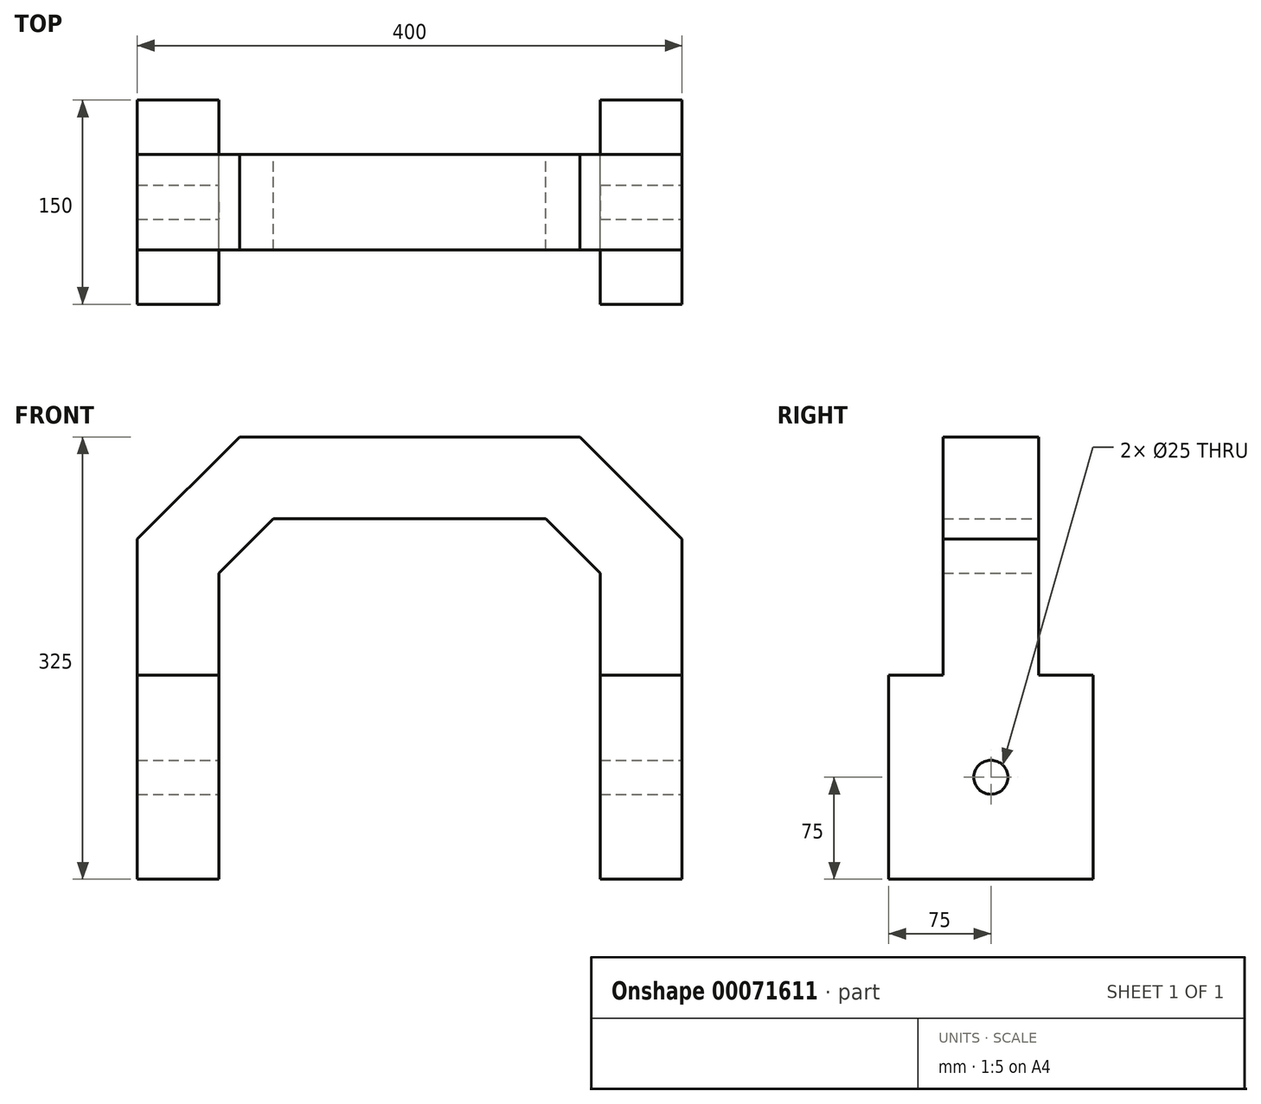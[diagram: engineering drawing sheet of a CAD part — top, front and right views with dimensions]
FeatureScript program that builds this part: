
annotation { "Feature Type Name" : "Feature", "Feature Type Description" : "" }
export const myFeature = defineFeature(function(context is Context, id is Id, definition is map)
    precondition{}
    {
        {
            var Q0;
            Q0=qCreatedBy(makeId("Front.planeOp"),FACE);
            var sketch = newSketch(context, id + "F0", { "sketchPlane" : qUnion([Q0])});
            skLineSegment(sketch, "E0", {"start": v(-140, 0) * mm, "end": v(-140, 150) * mm});
            skLineSegment(sketch, "E1", {"start": v(-140, 150) * mm, "end": v(-100, 190) * mm});
            skLineSegment(sketch, "E2", {"start": v(-100, 190) * mm, "end": v(100, 190) * mm});
            skLineSegment(sketch, "E3", {"start": v(100, 190) * mm, "end": v(140, 150) * mm});
            skLineSegment(sketch, "E4", {"start": v(140, 150) * mm, "end": v(140, 0) * mm});
            skLineSegment(sketch, "E5", {"start": v(140, 0) * mm, "end": v(200, 0) * mm});
            skLineSegment(sketch, "E6", {"start": v(200, 0) * mm, "end": v(200, 174.85) * mm});
            skLineSegment(sketch, "E7", {"start": v(200, 250) * mm, "end": v(124.85, 250) * mm, "construction": true});
            skLineSegment(sketch, "E8", {"start": v(-200, 0) * mm, "end": v(-140, 0) * mm});
            skLineSegment(sketch, "E9", {"start": v(-140, 0) * mm, "end": v(140, 0) * mm, "construction": true});
            skLineSegment(sketch, "E10", {"start": v(0, 0) * mm, "end": v(0, 190) * mm, "construction": true});
            skLineSegment(sketch, "E11", {"start": v(-140, 150) * mm, "end": v(140, 150) * mm, "construction": true});
            skLineSegment(sketch, "E12", {"start": v(-124.85, 250) * mm, "end": v(-200, 250) * mm, "construction": true});
            skLineSegment(sketch, "E13", {"start": v(-200, 174.85) * mm, "end": v(-200, 0) * mm});
            skLineSegment(sketch, "E14", {"start": v(124.85, 250) * mm, "end": v(-124.85, 250) * mm});
            skLineSegment(sketch, "E15", {"start": v(200, 174.85) * mm, "end": v(200, 250) * mm, "construction": true});
            skLineSegment(sketch, "E16", {"start": v(124.85, 250) * mm, "end": v(200, 174.85) * mm});
            skLineSegment(sketch, "E17", {"start": v(-200, 174.85) * mm, "end": v(-124.85, 250) * mm});
            skLineSegment(sketch, "E18", {"start": v(-200, 174.85) * mm, "end": v(-200, 250) * mm, "construction": true});
            skLineSegment(sketch, "E19", {"start": v(0, 190) * mm, "end": v(0, 250) * mm, "construction": true});
            skLineSegment(sketch, "E20", {"start": v(-100, 190) * mm, "end": v(-142.43, 232.43) * mm, "construction": true});
            skSolve(sketch);
        }
        {
            var Q0;
            Q0 = qSketchRegion(id + "F0", true);
            extrude(context, id + "F1", {"entities" : qUnion([Q0]), "depth" : 70 * mm});
        }
        {
            var Q0;
            Q0=makeQuery(id+"F1.opExtrude","SWEPT_FACE",FACE,{"disambiguationData":[OSD([sQuery(id+"F0.wireOp",EDGE,"E6")])]});
            var sketch = newSketch(context, id + "F2", { "sketchPlane" : qUnion([Q0])});
            skLineSegment(sketch, "E21.rect.bottom", {"start": v(40, -75) * mm, "end": v(-110, -75) * mm});
            skLineSegment(sketch, "E21.rect.top", {"start": v(40, 75) * mm, "end": v(-110, 75) * mm});
            skLineSegment(sketch, "E21.rect.left", {"start": v(40, -75) * mm, "end": v(40, 75) * mm});
            skLineSegment(sketch, "E21.rect.right", {"start": v(-110, -75) * mm, "end": v(-110, 75) * mm});
            skPoint(sketch, "E21.rect.middle", {"position": v(-35, 0) * mm});
            skSolve(sketch);
        }
        {
            var Q0;
            Q0 = qSketchRegion(id + "F2", true);
            var Q1;
            Q1=makeQuery(id+"F1.opExtrude","SWEPT_FACE",FACE,{"disambiguationData":[OSD([sQuery(id+"F0.wireOp",EDGE,"E4")])]});
            extrude(context, id + "F3", {"entities" : qUnion([Q0]), "operationType" : NewBodyOperationType.ADD, "endBound" : BoundingType.UP_TO_SURFACE, "oppositeDirection" : true, "endBoundEntityFace" : qUnion([Q1]), "depth" : 60 * mm});
        }
        {
            var Q0;
            Q0=makeQuery(id+"F1.opExtrude","SWEPT_FACE",FACE,{"disambiguationData":[OSD([sQuery(id+"F0.wireOp",EDGE,"E13")])]});
            var sketch = newSketch(context, id + "F4", { "sketchPlane" : qUnion([Q0])});
            skLineSegment(sketch, "E22.bottom", {"start": v(-40, 75) * mm, "end": v(110, 75) * mm});
            skLineSegment(sketch, "E22.top", {"start": v(-40, -75) * mm, "end": v(110, -75) * mm});
            skLineSegment(sketch, "E22.left", {"start": v(-40, 75) * mm, "end": v(-40, -75) * mm});
            skLineSegment(sketch, "E22.right", {"start": v(110, 75) * mm, "end": v(110, -75) * mm});
            skSolve(sketch);
        }
        {
            var Q0;
            Q0 = qSketchRegion(id + "F4", true);
            var Q1;
            Q1=makeQuery(id+"F1.opExtrude","SWEPT_FACE",FACE,{"disambiguationData":[OSD([sQuery(id+"F0.wireOp",EDGE,"E0")])]});
            extrude(context, id + "F5", {"entities" : qUnion([Q0]), "operationType" : NewBodyOperationType.ADD, "endBound" : BoundingType.UP_TO_SURFACE, "oppositeDirection" : true, "endBoundEntityFace" : qUnion([Q1]), "depth" : 25 * mm});
        }
        {
            var Q0;
            Q0=makeQuery(id+"F3.boolean.opBoolean","MERGE",FACE,{"derivedFrom":[makeQuery(id+"F1.opExtrude","SWEPT_FACE",FACE,{"disambiguationData":[OSD([sQuery(id+"F0.wireOp",EDGE,"E6")])]}),makeQuery(id+"F3.opExtrude","CAP_FACE",FACE,{"disambiguationData":[OSD([sQuery(id+"F2.wireOp",EDGE,"E21.rect.bottom"),sQuery(id+"F2.wireOp",EDGE,"E21.rect.top"),sQuery(id+"F2.wireOp",EDGE,"E21.rect.left"),sQuery(id+"F2.wireOp",EDGE,"E21.rect.right")])],"isStart":true})]});
            var sketch = newSketch(context, id + "F6", { "sketchPlane" : qUnion([Q0])});
            skCircle(sketch, "E23", {"center": v(-35, 0) * mm, "radius": 12.5 * mm});
            skLineSegment(sketch, "E24", {"start": v(-35, 0) * mm, "end": v(-35, -75) * mm, "construction": true});
            skSolve(sketch);
        }
        {
            var Q0;
            Q0 = qSketchRegion(id + "F6", true);
            extrude(context, id + "F7", {"entities" : qUnion([Q0]), "operationType" : NewBodyOperationType.REMOVE, "endBound" : BoundingType.THROUGH_ALL, "oppositeDirection" : true, "depth" : 25 * mm});
        }
    });
